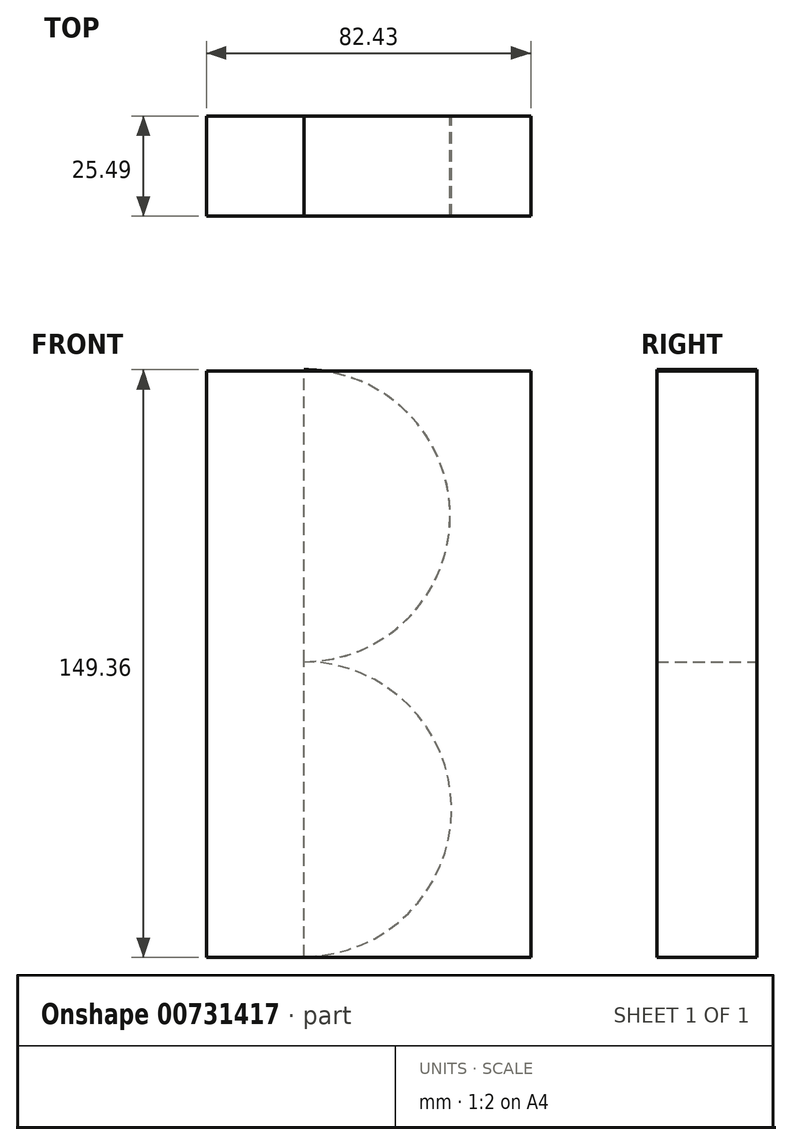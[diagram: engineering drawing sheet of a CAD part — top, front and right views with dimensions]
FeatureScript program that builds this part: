
annotation { "Feature Type Name" : "Feature", "Feature Type Description" : "" }
export const myFeature = defineFeature(function(context is Context, id is Id, definition is map)
    precondition{}
    {
        {
            var Q0;
            Q0=qCreatedBy(makeId("Front.planeOp"),FACE);
            var sketch = newSketch(context, id + "F0", { "sketchPlane" : qUnion([Q0])});
            skLineSegment(sketch, "E0", {"start": v(-57.6, -76.56) * mm, "end": v(-57.6, 74.87) * mm});
            skArc(sketch, "E1", {"start": v(-57.6, 74.87) * mm, "mid": v(-20.5, 37.77) * mm, "end": v(-57.6, 0.68) * mm});
            skArc(sketch, "E2", {"start": v(-57.6, 0.68) * mm, "mid": v(-20.16, -36.76) * mm, "end": v(-57.6, -74.2) * mm});
            skSolve(sketch);
        }
        {
            var Q0;
            Q0 = qSketchRegion(id + "F0", true);
            extrude(context, id + "F1", {"entities" : qUnion([Q0]), "depth" : 25.4 * mm, "offsetDistance" : 25.4 * mm});
        }
        {
            var Q0;
            Q0=qCreatedBy(makeId("Right.planeOp"),FACE);
            var sketch = newSketch(context, id + "F2", { "sketchPlane" : qUnion([Q0])});
            skLineSegment(sketch, "E3.bottom", {"start": v(-25.42, -74.49) * mm, "end": v(0.07, -74.49) * mm});
            skLineSegment(sketch, "E3.top", {"start": v(-25.42, 74.49) * mm, "end": v(0.07, 74.49) * mm});
            skLineSegment(sketch, "E3.left", {"start": v(-25.42, -74.49) * mm, "end": v(-25.42, 74.49) * mm});
            skLineSegment(sketch, "E3.right", {"start": v(0.07, -74.49) * mm, "end": v(0.07, 74.49) * mm});
            skPoint(sketch, "E3.middle", {"position": v(-12.68, 0) * mm});
            skSolve(sketch);
        }
        {
            var Q0;
            Q0 = qSketchRegion(id + "F2", true);
            extrude(context, id + "F3", {"entities" : qUnion([Q0]), "oppositeDirection" : true, "depth" : 82.43 * mm, "offsetDistance" : 25.4 * mm});
        }
    });
